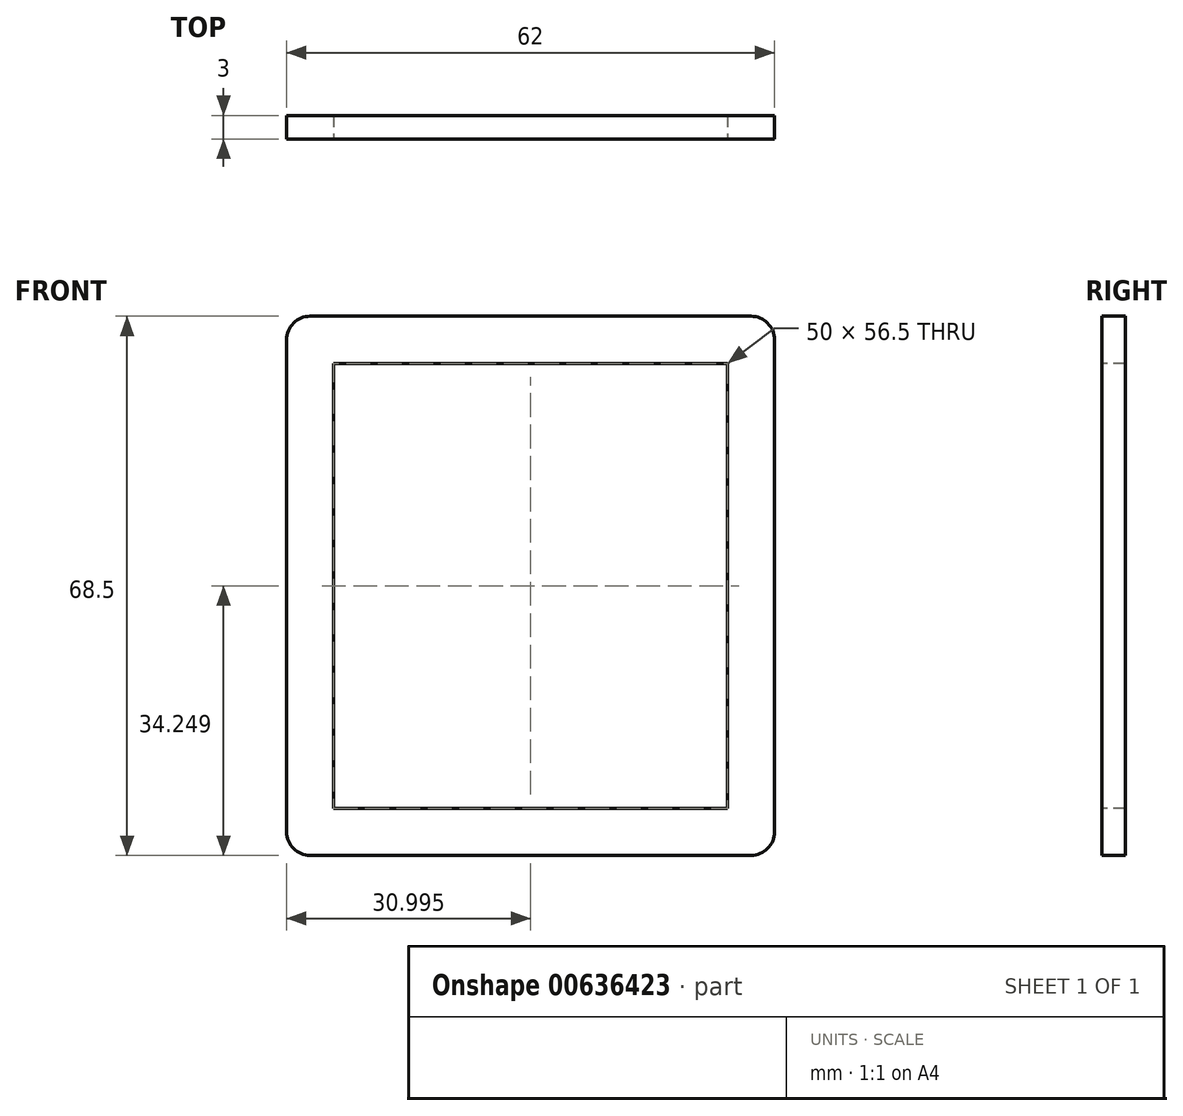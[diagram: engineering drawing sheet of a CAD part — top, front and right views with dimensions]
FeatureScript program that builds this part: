
annotation { "Feature Type Name" : "Feature", "Feature Type Description" : "" }
export const myFeature = defineFeature(function(context is Context, id is Id, definition is map)
    precondition{}
    {
        {
            var Q0;
            Q0=qCreatedBy(makeId("Front.planeOp"),FACE);
            var sketch = newSketch(context, id + "F0", { "sketchPlane" : qUnion([Q0])});
            skLineSegment(sketch, "E0.bottom", {"start": v(-41.86, 37.54) * mm, "end": v(14.14, 37.54) * mm});
            skLineSegment(sketch, "E0.top", {"start": v(-41.86, -30.96) * mm, "end": v(14.14, -30.96) * mm});
            skLineSegment(sketch, "E0.left", {"start": v(-44.86, 34.54) * mm, "end": v(-44.86, -27.96) * mm});
            skLineSegment(sketch, "E0.right", {"start": v(17.14, 34.54) * mm, "end": v(17.14, -27.96) * mm});
            skPoint(sketch, "E1.visualSharp", {"position": v(-44.86, 37.54) * mm});
            skArc(sketch, "E1.filletArc", {"start": v(-41.86, 37.54) * mm, "mid": v(-43.99, 36.66) * mm, "end": v(-44.86, 34.54) * mm});
            skPoint(sketch, "E2.visualSharp", {"position": v(17.14, 37.54) * mm});
            skArc(sketch, "E2.filletArc", {"start": v(17.14, 34.54) * mm, "mid": v(16.26, 36.66) * mm, "end": v(14.14, 37.54) * mm});
            skPoint(sketch, "E3.visualSharp", {"position": v(17.14, -30.96) * mm});
            skArc(sketch, "E3.filletArc", {"start": v(14.14, -30.96) * mm, "mid": v(16.26, -30.08) * mm, "end": v(17.14, -27.96) * mm});
            skPoint(sketch, "E4.visualSharp", {"position": v(-44.86, -30.96) * mm});
            skArc(sketch, "E4.filletArc", {"start": v(-44.86, -27.96) * mm, "mid": v(-43.99, -30.08) * mm, "end": v(-41.86, -30.96) * mm});
            skSolve(sketch);
        }
        {
            var Q0;
            Q0=qSketchRegion(id+"F0",true);
            extrude(context, id + "F1", {"entities" : qUnion([Q0]), "depth" : 3 * mm, "offsetDistance" : 25 * mm});
        }
        {
            var Q0;
            Q0=makeQuery(id+"F1.opExtrude","CAP_FACE",FACE,{"disambiguationData":[OSD([sQuery(id+"F0.wireOp",EDGE,"E0.bottom"),sQuery(id+"F0.wireOp",EDGE,"E0.top"),sQuery(id+"F0.wireOp",EDGE,"E0.left"),sQuery(id+"F0.wireOp",EDGE,"E0.right"),sQuery(id+"F0.wireOp",EDGE,"E1.filletArc"),sQuery(id+"F0.wireOp",EDGE,"E2.filletArc"),sQuery(id+"F0.wireOp",EDGE,"E3.filletArc"),sQuery(id+"F0.wireOp",EDGE,"E4.filletArc")])],"isStart":false});
            var sketch = newSketch(context, id + "F2", { "sketchPlane" : qUnion([Q0])});
            skLineSegment(sketch, "E5.bottom", {"start": v(-38.86, 31.54) * mm, "end": v(11.14, 31.54) * mm});
            skLineSegment(sketch, "E5.top", {"start": v(-38.86, -24.96) * mm, "end": v(11.14, -24.96) * mm});
            skLineSegment(sketch, "E5.left", {"start": v(-38.86, 31.54) * mm, "end": v(-38.86, -24.96) * mm});
            skLineSegment(sketch, "E5.right", {"start": v(11.14, 31.54) * mm, "end": v(11.14, -24.96) * mm});
            skSolve(sketch);
        }
        {
            var Q0;
            Q0=makeQuery(id+"F2.imprint","IMPRINT",FACE,{"disambiguationData":[TD([[makeQuery(id+"F2.imprint","IMPRINT",EDGE,{"derivedFrom":sQuery(id+"F2.wireOp",EDGE,"E5.bottom")}),-1.0]])]});
            extrude(context, id + "F3", {"entities" : qUnion([Q0]), "operationType" : NewBodyOperationType.REMOVE, "oppositeDirection" : true, "depth" : 25 * mm, "offsetDistance" : 25 * mm});
        }
    });
